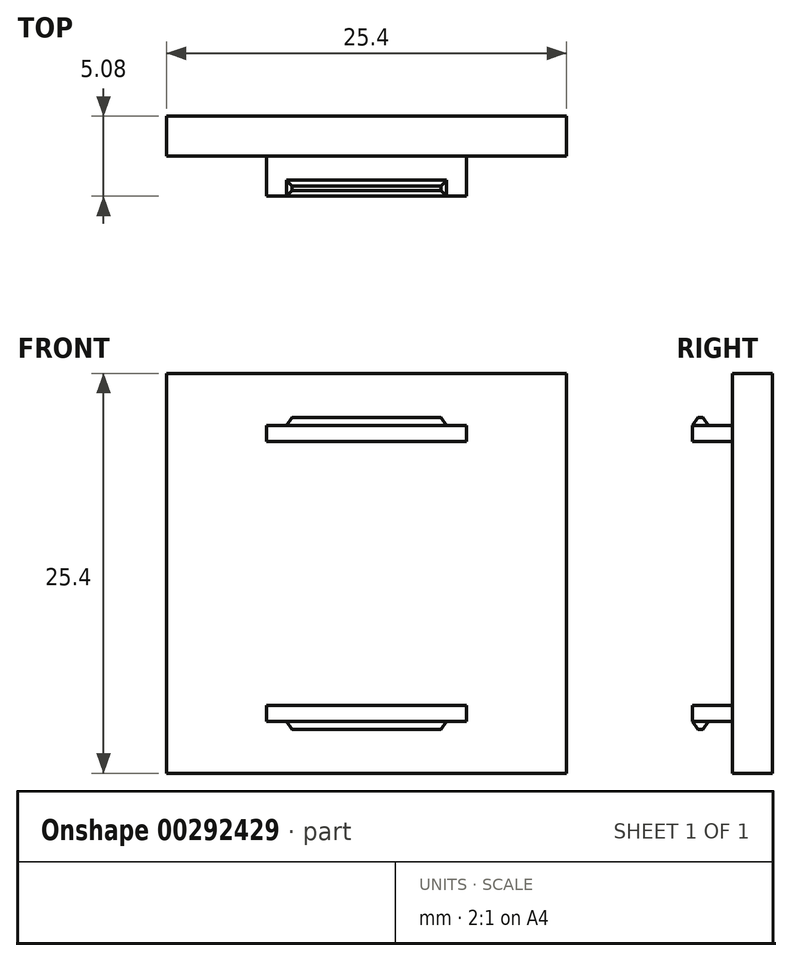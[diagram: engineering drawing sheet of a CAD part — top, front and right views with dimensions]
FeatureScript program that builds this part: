
annotation { "Feature Type Name" : "Feature", "Feature Type Description" : "" }
export const myFeature = defineFeature(function(context is Context, id is Id, definition is map)
    precondition{}
    {
        {
            var Q0;
            Q0=qCreatedBy(makeId("Front.planeOp"),FACE);
            var sketch = newSketch(context, id + "F0", { "sketchPlane" : qUnion([Q0])});
            skLineSegment(sketch, "E0.bottom", {"start": v(-12.7, 12.7) * mm, "end": v(12.7, 12.7) * mm});
            skLineSegment(sketch, "E0.top", {"start": v(-12.7, -12.7) * mm, "end": v(12.7, -12.7) * mm});
            skLineSegment(sketch, "E0.left", {"start": v(-12.7, 12.7) * mm, "end": v(-12.7, -12.7) * mm});
            skLineSegment(sketch, "E0.right", {"start": v(12.7, 12.7) * mm, "end": v(12.7, -12.7) * mm});
            skPoint(sketch, "E1", {"position": v(-12.7, 12.7) * mm});
            skPoint(sketch, "E2.MirrorP", {"position": v(0, 8.89) * mm});
            skLineSegment(sketch, "E3.bottom", {"start": v(6.35, 9.4) * mm, "end": v(-6.35, 9.4) * mm});
            skLineSegment(sketch, "E3.top", {"start": v(6.35, 8.38) * mm, "end": v(-6.35, 8.38) * mm});
            skLineSegment(sketch, "E3.left", {"start": v(6.35, 9.4) * mm, "end": v(6.35, 8.38) * mm});
            skLineSegment(sketch, "E3.right", {"start": v(-6.35, 9.4) * mm, "end": v(-6.35, 8.38) * mm});
            skSolve(sketch);
        }
        {
            var Q0;
            Q0=makeQuery(id+"F0.imprint","IMPRINT",FACE,{"disambiguationData":[TD([[makeQuery(id+"F0.imprint","IMPRINT",EDGE,{"derivedFrom":sQuery(id+"F0.wireOp",EDGE,"E3.bottom")}),1.0]])]});
            extrude(context, id + "F1", {"entities" : qUnion([Q0]), "depth" : 2.54 * mm, "hasSecondDirection" : true, "secondDirectionOppositeDirection" : true, "secondDirectionDepth" : 2.54 * mm});
        }
        {
            var Q0;
            Q0=makeQuery(id+"F0.imprint","IMPRINT",FACE,{"disambiguationData":[TD([[makeQuery(id+"F0.imprint","IMPRINT",EDGE,{"derivedFrom":sQuery(id+"F0.wireOp",EDGE,"E0.bottom")}),-1.0]])]});
            extrude(context, id + "F2", {"entities" : qUnion([Q0]), "operationType" : NewBodyOperationType.ADD, "oppositeDirection" : true, "depth" : 2.54 * mm});
        }
        {
            var Q0;
            Q0=makeQuery(id+"F1.opExtrude","SWEPT_FACE",FACE,{"disambiguationData":[OSD([sQuery(id+"F0.wireOp",EDGE,"E3.bottom")])]});
            var sketch = newSketch(context, id + "F3", { "sketchPlane" : qUnion([Q0])});
            skPoint(sketch, "E4", {"position": v(0, -2.03) * mm});
            skPoint(sketch, "E4.positionSnap0", {"position": v(0, -2.54) * mm});
            skLineSegment(sketch, "E5.bottom", {"start": v(-5.08, -1.52) * mm, "end": v(5.08, -1.52) * mm});
            skLineSegment(sketch, "E5.top", {"start": v(-5.08, -2.54) * mm, "end": v(5.08, -2.54) * mm});
            skLineSegment(sketch, "E5.left", {"start": v(-5.08, -1.52) * mm, "end": v(-5.08, -2.54) * mm});
            skLineSegment(sketch, "E5.right", {"start": v(5.08, -1.52) * mm, "end": v(5.08, -2.54) * mm});
            skSolve(sketch);
        }
        {
            var Q0;
            Q0=makeQuery(id+"F3.imprint","IMPRINT",FACE,{"disambiguationData":[TD([[makeQuery(id+"F3.imprint","IMPRINT",EDGE,{"derivedFrom":sQuery(id+"F3.wireOp",EDGE,"E5.bottom")}),-1.0]])]});
            extrude(context, id + "F4", {"entities" : qUnion([Q0]), "operationType" : NewBodyOperationType.ADD, "depth" : 0.5 * mm, "hasDraft" : true, "draftAngle" : 35 * degree, "draftPullDirection" : true});
        }
        {
            var Q0;
            Q0=makeQuery(id+"F1.opExtrude","SWEPT_BODY",BODY,{"disambiguationData":[OSD([sQuery(id+"F0.wireOp",EDGE,"E3.bottom"),sQuery(id+"F0.wireOp",EDGE,"E3.top"),sQuery(id+"F0.wireOp",EDGE,"E3.left"),sQuery(id+"F0.wireOp",EDGE,"E3.right")])]});
            var Q1;
            Q1=qCreatedBy(makeId("Top.planeOp"),FACE);
            mirror(context, id + "F5", {"operationType" : NewBodyOperationType.ADD, "entities" : qUnion([Q0]), "mirrorPlane" : qUnion([Q1])});
        }
    });
